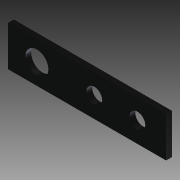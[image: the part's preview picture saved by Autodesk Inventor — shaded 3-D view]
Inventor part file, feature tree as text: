
AUTODESK INVENTOR PART (.ipt)
format: ipt  version: 2011 SP1 (Build 150282100, 282)  size: 78,336 bytes
history: native  units: mm
features: other x7, extrude x1, sketch x1
ambient origin geometry x8: Origin, YZ Plane, XZ Plane, XY Plane, X Axis, Y Axis, Z Axis, Center Point
bodies: Solid1 (feature_tree)
feature tree (9):
  extrude  "Extrusion1"  [1 undecoded]
  other  "PLATE_BUFFER_XY"
  other  "PLATE_BUFFER_YZ"
  other  "PLATE_BUFFER_ZX"
  other  "PLATE_BUFFER_X"
  other  "PLATE_BUFFER_Y"
  other  "PLATE_BUFFER_Z"
  other  "PLATE_BUFFER_Center"
  sketch  "Sketch_1"  dims[d0=2.0mm d1=0.0mm]
note: 1 required parameter value undecoded (feature->parameter linkage not recoverable at this tier; creation-order binding heuristic only, values carry confidence <= 0.55)
